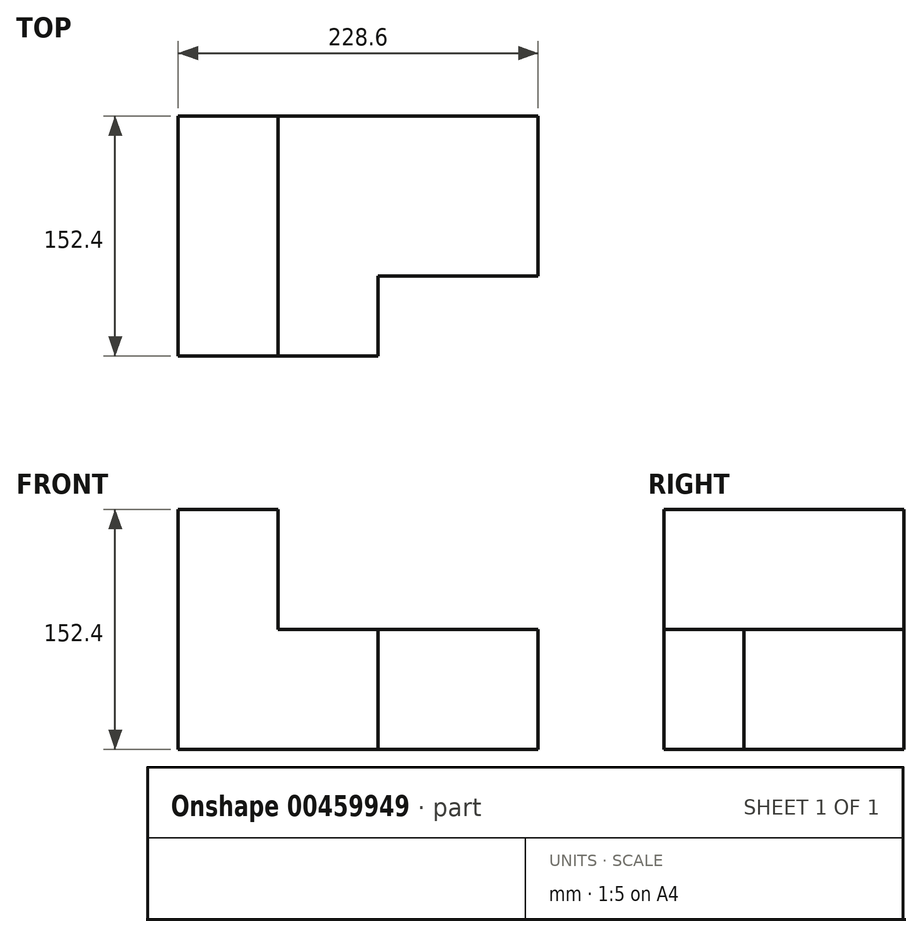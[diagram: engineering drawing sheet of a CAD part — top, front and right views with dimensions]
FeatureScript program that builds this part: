
annotation { "Feature Type Name" : "Feature", "Feature Type Description" : "" }
export const myFeature = defineFeature(function(context is Context, id is Id, definition is map)
    precondition{}
    {
        {
            var Q0;
            Q0=qCreatedBy(makeId("Front.planeOp"),FACE);
            var sketch = newSketch(context, id + "F0", { "sketchPlane" : qUnion([Q0])});
            skLineSegment(sketch, "E0", {"start": v(-182.47, 0) * mm, "end": v(-182.47, 152.4) * mm});
            skLineSegment(sketch, "E1", {"start": v(-118.97, 152.4) * mm, "end": v(-182.47, 152.4) * mm});
            skLineSegment(sketch, "E2", {"start": v(-118.97, 152.4) * mm, "end": v(-118.97, 76.2) * mm});
            skLineSegment(sketch, "E3", {"start": v(46.13, 76.2) * mm, "end": v(-118.97, 76.2) * mm});
            skLineSegment(sketch, "E4", {"start": v(46.13, 76.2) * mm, "end": v(46.13, 0) * mm});
            skLineSegment(sketch, "E5", {"start": v(-182.47, 0) * mm, "end": v(46.13, 0) * mm});
            skSolve(sketch);
        }
        {
            var Q0;
            Q0 = qSketchRegion(id + "F0", true);
            extrude(context, id + "F1", {"entities" : qUnion([Q0]), "depth" : 152.4 * mm});
        }
        {
            var Q0;
            Q0=makeQuery(id+"F1.opExtrude","CAP_FACE",FACE,{"disambiguationData":[OSD([sQuery(id+"F0.wireOp",EDGE,"E0"),sQuery(id+"F0.wireOp",EDGE,"E1"),sQuery(id+"F0.wireOp",EDGE,"E2"),sQuery(id+"F0.wireOp",EDGE,"E3"),sQuery(id+"F0.wireOp",EDGE,"E4"),sQuery(id+"F0.wireOp",EDGE,"E5")])],"isStart":false});
            var sketch = newSketch(context, id + "F2", { "sketchPlane" : qUnion([Q0])});
            skLineSegment(sketch, "E6", {"start": v(46.13, 76.2) * mm, "end": v(46.13, 0) * mm});
            skLineSegment(sketch, "E7", {"start": v(46.13, 0) * mm, "end": v(-55.47, 0) * mm});
            skLineSegment(sketch, "E8", {"start": v(46.13, 76.2) * mm, "end": v(-55.47, 76.2) * mm});
            skLineSegment(sketch, "E9", {"start": v(-55.47, 76.2) * mm, "end": v(-55.47, 0) * mm});
            skSolve(sketch);
        }
        {
            var Q0;
            Q0 = qSketchRegion(id + "F2", true);
            extrude(context, id + "F3", {"entities" : qUnion([Q0]), "operationType" : NewBodyOperationType.REMOVE, "oppositeDirection" : true, "depth" : 50.8 * mm});
        }
    });
